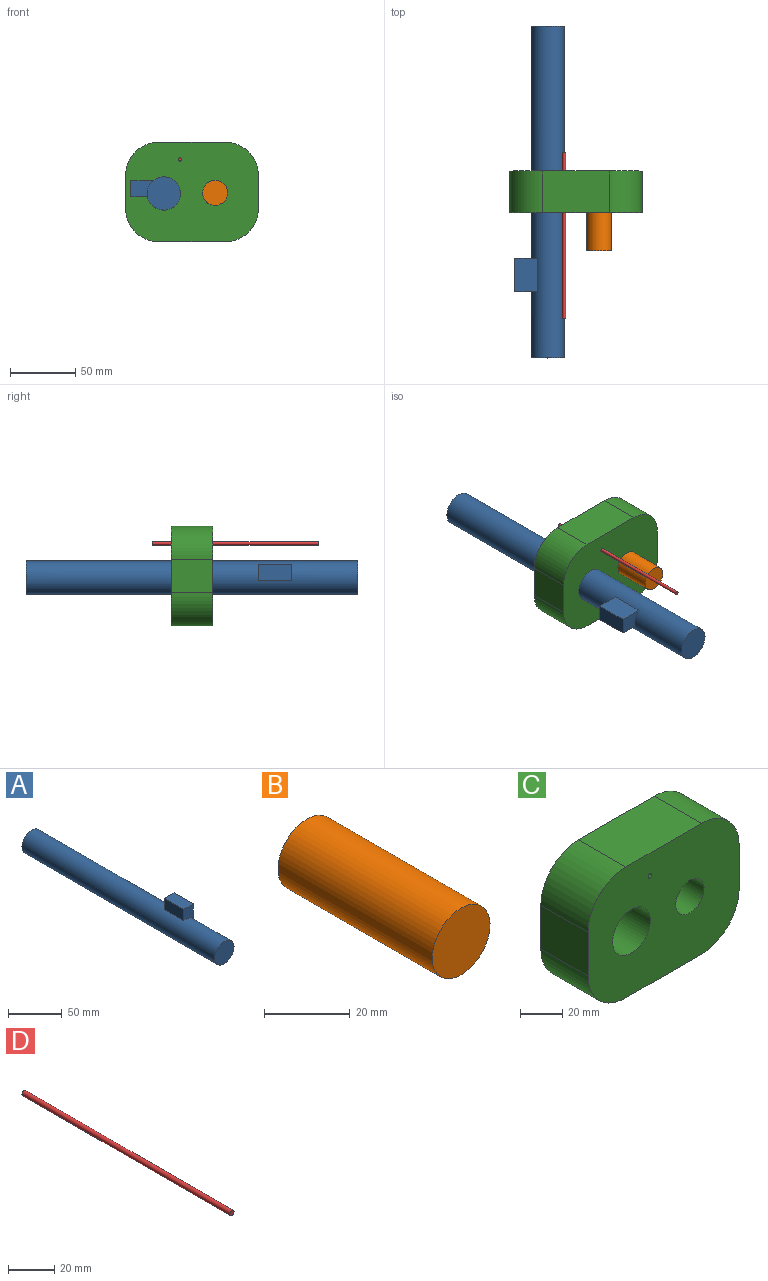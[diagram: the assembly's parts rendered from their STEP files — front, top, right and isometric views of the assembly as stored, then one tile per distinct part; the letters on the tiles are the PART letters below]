
ASSEMBLY  parts=4 mates=4
PART A: 8 faces, bbox 25.4x254x37.9 mm
  f0: cylinder r=12.7mm len=254mm, axis (0,1,0), area 19912mm2, adj f1,f2,f3,f4,f6,f7
  f1: plane 25.4x25.4mm, normal (0,-1,0), area 506.7mm2, adj f0
  f2: plane 25.4x25.4mm, normal (0,1,0), area 506.7mm2, adj f0
  f3: plane 25.4x12.8mm, normal (-1,0,0), area 325mm2, adj f0,f5,f6,f7
  f4: plane 25.4x17.25mm, normal (1,0,0), area 438mm2, adj f0,f5,f6,f7
  f5: plane 25.4x12.56mm, normal (0,0,1), area 319.1mm2, adj f3,f4,f6,f7
  f6: plane 17.25x12.56mm, normal (0,-1,0), area 171.6mm2, adj f0,f3,f4,f5
  f7: plane 17.25x12.56mm, normal (0,1,0), area 171.6mm2, adj f0,f3,f4,f5
PART B: 3 faces, bbox 19.1x50.8x19.1 mm
  f0: cylinder r=9.53mm len=50.8mm, axis (0,1,0), area 3040.2mm2, adj f1,f2
  f1: plane 19.05x19.05mm, normal (0,-1,0), area 285mm2, adj f0
  f2: plane 19.05x19.05mm, normal (0,1,0), area 285mm2, adj f0
PART C: 13 faces, bbox 101.6x31.8x76.2 mm
  f0: plane 50.8x31.75mm, normal (0,0,1), area 1612.9mm2, adj f7,f8,f9,f12
  f1: plane 31.75x25.4mm, normal (-1,0,0), area 806.5mm2, adj f7,f8,f9,f10
  f2: plane 50.8x31.75mm, normal (0,0,-1), area 1612.9mm2, adj f7,f8,f10,f11
  f3: cylinder r=12.7mm len=31.75mm, axis (0,1,0), area 2533.5mm2, adj f7,f8
  f4: cylinder r=9.53mm len=31.75mm, axis (0,1,0), area 1900.2mm2, adj f7,f8
  f5: cylinder r=1.27mm len=31.75mm, axis (0,1,0), area 253.4mm2, adj f7,f8
  f6: plane 31.75x25.4mm, normal (1,0,0), area 806.5mm2, adj f7,f8,f11,f12
  f7: plane 101.6x76.2mm, normal (0,-1,0), area 6391.3mm2, adj f0,f1,f2,f3,f4,f5,f6,f9
  f8: plane 101.6x76.2mm, normal (0,1,0), area 6391.3mm2, adj f0,f1,f2,f3,f4,f5,f6,f9
  f9: cylinder r=25.4mm len=31.75mm, axis (0,-1,0), area 1266.8mm2, adj f0,f1,f7,f8
  f10: cylinder r=25.4mm len=31.75mm, axis (0,1,0), area 1266.8mm2, adj f1,f2,f7,f8
  f11: cylinder r=25.4mm len=31.75mm, axis (0,-1,0), area 1266.8mm2, adj f2,f6,f7,f8
  f12: cylinder r=25.4mm len=31.75mm, axis (0,1,0), area 1266.8mm2, adj f0,f6,f7,f8
PART D: 3 faces, bbox 2.5x127x2.5 mm
  f0: cylinder r=1.27mm len=127mm, axis (0,1,0), area 1013.4mm2, adj f1,f2
  f1: plane 2.54x2.54mm, normal (0,-1,0), area 5.1mm2, adj f0
  f2: plane 2.54x2.54mm, normal (0,1,0), area 5.1mm2, adj f0
PLACE A rot(axis=(0,-1,0),90deg) t=(-26.38,110.06,23.79)mm
PLACE B rot(axis=(0,1,0),22.9deg) t=(48.79,-11.21,-10.48)mm
PLACE C t=(1.35,-0.91,3.8)mm fixed
PLACE D rot(axis=(0,-1,0),70.7deg) t=(46.07,13.34,61.33)mm
MATE cylindrical C.f3 <-> A.f0  axis (0,-1,0) through (-26.38,-32.66,-2.33)mm
MATE parallel A.f5 <-> C.f1  axis (-1,0,0) through (-51.6,-80.44,1.28)mm
MATE cylindrical C.f4 <-> B.f0  axis (0,1,0) through (12.86,-16.79,-1.84)mm
MATE cylindrical D.f0 <-> C.f5  axis (0,1,0) through (-13.92,-50.16,23.76)mm
